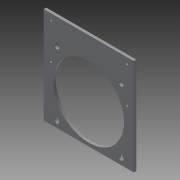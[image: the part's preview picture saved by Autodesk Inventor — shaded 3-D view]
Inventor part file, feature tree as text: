
AUTODESK INVENTOR PART (.ipt)
format: ipt  version: 2014 (Build 180170000, 170)  size: 114,176 bytes
history: native  units: mm
features: extrude x3, sketch x3
ambient origin geometry x8: Origin, YZ Plane, XZ Plane, XY Plane, X Axis, Y Axis, Z Axis, Center Point
bodies: Solid1 (feature_tree)
feature tree (6):
  extrude  "Extrusion1"  Depth=70.0mm
  extrude  "Extrusion2"  Depth=2.0mm
  extrude  "Extrusion5"  Depth=10.0mm
  sketch  "Sketch1"  dims[d0=75.0mm d1=70.0mm]
  sketch  "Sketch2"  dims[d2=2.0mm d3=0.0mm d7=4.0mm]
  sketch  "Sketch5"  dims[d8=10.0mm d9=0.0mm d42=20.0mm d44=50.0mm d45=20.0mm d47=50.0mm d56=55.0mm d57=2.0mm d58=4.5mm d59=20.0mm d61=59.0mm d62=20.0mm d64=28.0mm d68=59.0mm d71=60.0mm d72=60.0mm d73=30.0mm d74=5.0mm d75=55.0mm d76=10.0mm d77=0.0mm]
